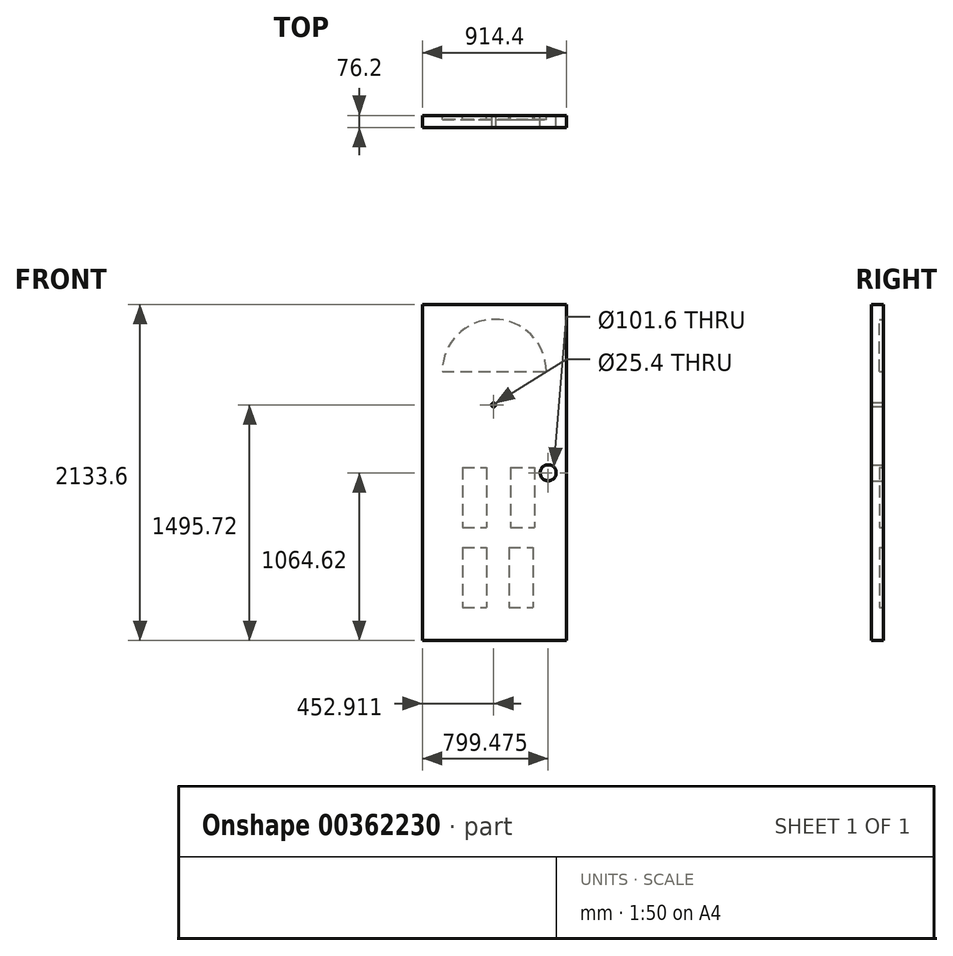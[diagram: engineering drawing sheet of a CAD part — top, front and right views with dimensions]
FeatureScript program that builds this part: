
annotation { "Feature Type Name" : "Feature", "Feature Type Description" : "" }
export const myFeature = defineFeature(function(context is Context, id is Id, definition is map)
    precondition{}
    {
        {
            var Q0;
            Q0=qCreatedBy(makeId("Front.planeOp"),FACE);
            var sketch = newSketch(context, id + "F0", { "sketchPlane" : qUnion([Q0])});
            skLineSegment(sketch, "E0", {"start": v(0, 2133.6) * mm, "end": v(0, 0) * mm});
            skLineSegment(sketch, "E1", {"start": v(0, 2133.6) * mm, "end": v(914.4, 2133.6) * mm});
            skLineSegment(sketch, "E2", {"start": v(914.4, 0) * mm, "end": v(914.4, 2133.6) * mm});
            skLineSegment(sketch, "E3", {"start": v(914.4, 0) * mm, "end": v(0, 0) * mm});
            skSolve(sketch);
        }
        {
            var Q0;
            Q0=qCreatedBy(makeId("Front.planeOp"),FACE);
            var sketch = newSketch(context, id + "F1", { "sketchPlane" : qUnion([Q0])});
            skLineSegment(sketch, "E4", {"start": v(127, 1708.72) * mm, "end": v(787.4, 1708.72) * mm});
            skArc(sketch, "E5", {"start": v(787.4, 1708.72) * mm, "mid": v(457.2, 2038.92) * mm, "end": v(127, 1708.72) * mm});
            skSolve(sketch);
        }
        {
            var Q0;
            Q0=qCreatedBy(makeId("Front.planeOp"),FACE);
            var sketch = newSketch(context, id + "F2", { "sketchPlane" : qUnion([Q0])});
            skLineSegment(sketch, "E6.bottom", {"start": v(255.15, 1098.08) * mm, "end": v(407.55, 1098.08) * mm});
            skLineSegment(sketch, "E6.top", {"start": v(255.15, 717.08) * mm, "end": v(407.55, 717.08) * mm});
            skLineSegment(sketch, "E6.left", {"start": v(255.15, 1098.08) * mm, "end": v(255.15, 717.08) * mm});
            skLineSegment(sketch, "E6.right", {"start": v(407.55, 1098.08) * mm, "end": v(407.55, 717.08) * mm});
            skLineSegment(sketch, "E7.bottom", {"start": v(559.95, 1098.08) * mm, "end": v(712.35, 1098.08) * mm});
            skLineSegment(sketch, "E7.top", {"start": v(559.95, 717.08) * mm, "end": v(712.35, 717.08) * mm});
            skLineSegment(sketch, "E7.left", {"start": v(559.95, 1098.08) * mm, "end": v(559.95, 717.08) * mm});
            skLineSegment(sketch, "E7.right", {"start": v(712.35, 1098.08) * mm, "end": v(712.35, 717.08) * mm});
            skLineSegment(sketch, "E8.bottom", {"start": v(255.15, 590.08) * mm, "end": v(407.55, 590.08) * mm});
            skLineSegment(sketch, "E8.top", {"start": v(255.15, 209.08) * mm, "end": v(407.55, 209.08) * mm});
            skLineSegment(sketch, "E8.left", {"start": v(255.15, 590.08) * mm, "end": v(255.15, 209.08) * mm});
            skLineSegment(sketch, "E8.right", {"start": v(407.55, 590.08) * mm, "end": v(407.55, 209.08) * mm});
            skLineSegment(sketch, "E9.bottom", {"start": v(550.2, 590.46) * mm, "end": v(702.6, 590.46) * mm});
            skLineSegment(sketch, "E9.top", {"start": v(550.2, 209.46) * mm, "end": v(702.6, 209.46) * mm});
            skLineSegment(sketch, "E9.left", {"start": v(550.2, 590.46) * mm, "end": v(550.2, 209.46) * mm});
            skLineSegment(sketch, "E9.right", {"start": v(702.6, 590.46) * mm, "end": v(702.6, 209.46) * mm});
            skSolve(sketch);
        }
        {
            var Q0;
            Q0=qCreatedBy(makeId("Front.planeOp"),FACE);
            var sketch = newSketch(context, id + "F3", { "sketchPlane" : qUnion([Q0])});
            skCircle(sketch, "E10", {"center": v(799.48, 1064.62) * mm, "radius": 88.9 * mm});
            skSolve(sketch);
        }
        {
            var Q0;
            Q0 = qSketchRegion(id + "F0", true);
            extrude(context, id + "F4", {"entities" : qUnion([Q0]), "depth" : 76.2 * mm});
        }
        {
            var Q0;
            Q0=makeQuery(id+"F4.opExtrude","CAP_FACE",FACE,{"disambiguationData":[OSD([sQuery(id+"F0.wireOp",EDGE,"E0"),sQuery(id+"F0.wireOp",EDGE,"E1"),sQuery(id+"F0.wireOp",EDGE,"E2"),sQuery(id+"F0.wireOp",EDGE,"E3")])],"isStart":false});
            var sketch = newSketch(context, id + "F5", { "sketchPlane" : qUnion([Q0])});
            skCircle(sketch, "E11", {"center": v(452.91, 1495.72) * mm, "radius": 60.07 * mm});
            skSolve(sketch);
        }
        {
            var Q0;
            Q0=sQuery(id+"F3.wireOp",VERTEX,"E10.center");
            var Q1;
            Q1=makeQuery(id+"F4.opExtrude","SWEPT_BODY",BODY,{"disambiguationData":[OSD([sQuery(id+"F0.wireOp",EDGE,"E0"),sQuery(id+"F0.wireOp",EDGE,"E1"),sQuery(id+"F0.wireOp",EDGE,"E2"),sQuery(id+"F0.wireOp",EDGE,"E3")])]});
            hole(context, id + "F6", {"style" : HoleStyle.SIMPLE, "endStyle" : HoleEndStyle.THROUGH, "oppositeDirection" : true, "holeDiameter" : 101.6 * mm, "isTappedThrough" : true, "tappedDepth" : 12.7 * mm, "tapClearance" : 3, "locations" : qUnion([Q0]), "scope" : qUnion([Q1])});
        }
        {
            var Q0;
            Q0=sQuery(id+"F5.wireOp",VERTEX,"E11.center");
            var Q1;
            Q1=makeQuery(id+"F4.opExtrude","SWEPT_BODY",BODY,{"disambiguationData":[OSD([sQuery(id+"F0.wireOp",EDGE,"E0"),sQuery(id+"F0.wireOp",EDGE,"E1"),sQuery(id+"F0.wireOp",EDGE,"E2"),sQuery(id+"F0.wireOp",EDGE,"E3")])]});
            hole(context, id + "F7", {"style" : HoleStyle.SIMPLE, "endStyle" : HoleEndStyle.THROUGH, "holeDiameter" : 25.4 * mm, "isTappedThrough" : true, "tappedDepth" : 12.7 * mm, "tapClearance" : 3, "locations" : qUnion([Q0]), "scope" : qUnion([Q1])});
        }
        {
            var Q0;
            Q0 = qSketchRegion(id + "F1", true);
            extrude(context, id + "F8", {"entities" : qUnion([Q0]), "operationType" : NewBodyOperationType.REMOVE, "depth" : 25.4 * mm});
        }
        {
            var Q0;
            Q0 = qSketchRegion(id + "F2", true);
            extrude(context, id + "F9", {"entities" : qUnion([Q0]), "operationType" : NewBodyOperationType.REMOVE, "depth" : 25.4 * mm});
        }
    });
